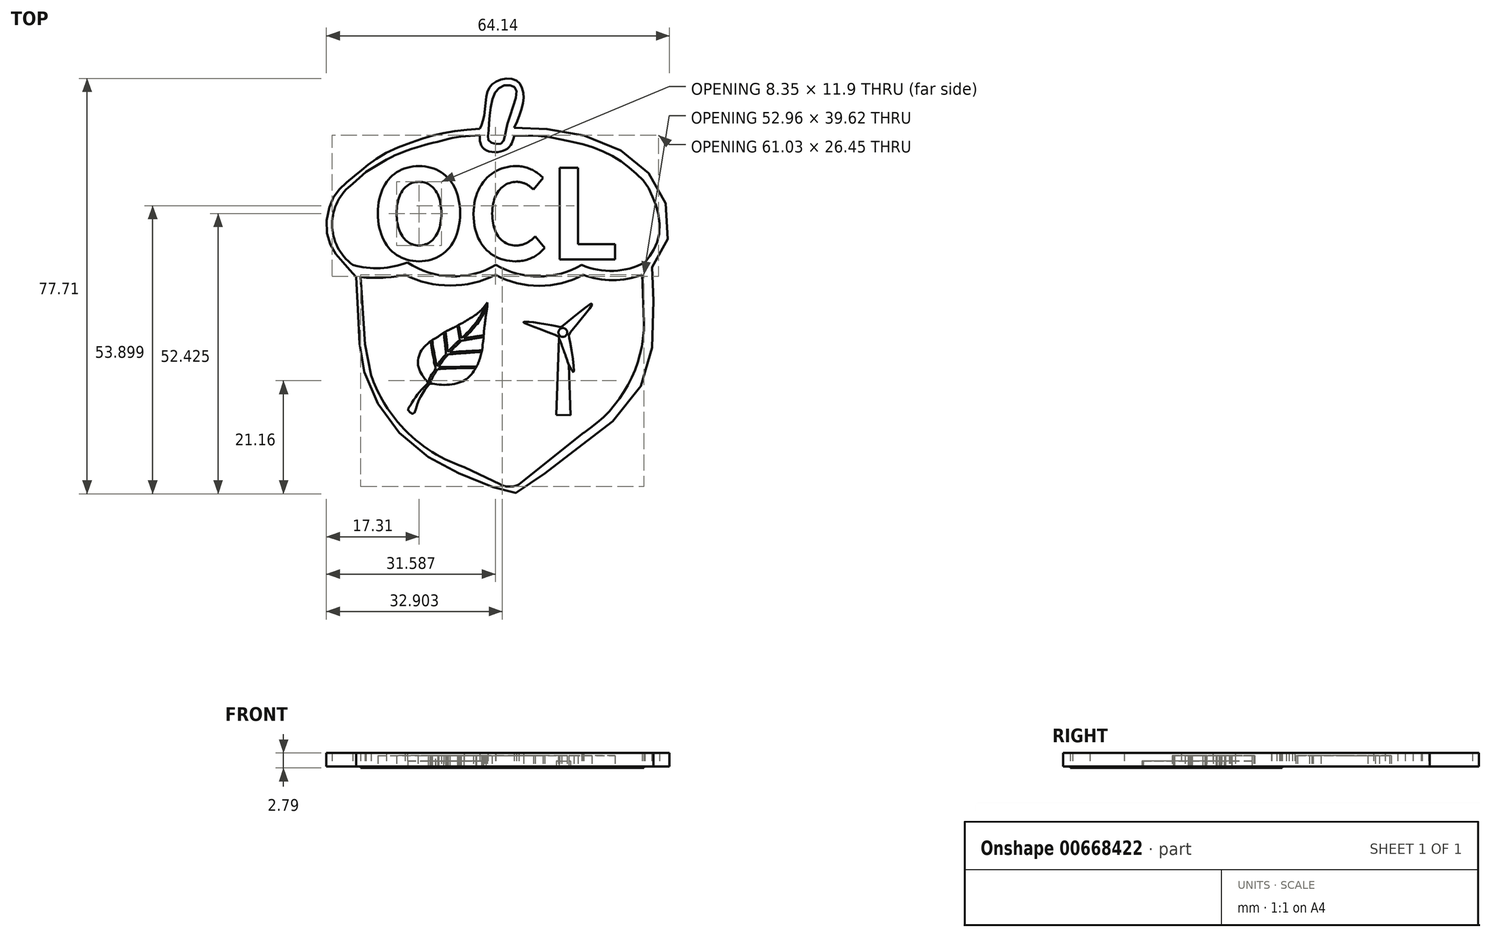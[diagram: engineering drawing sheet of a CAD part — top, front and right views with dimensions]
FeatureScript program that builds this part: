
annotation { "Feature Type Name" : "Feature", "Feature Type Description" : "" }
export const myFeature = defineFeature(function(context is Context, id is Id, definition is map)
    precondition{}
    {
        {
            var Q0;
            Q0=qCreatedBy(makeId("Top.planeOp"),FACE);
            var sketch = newSketch(context, id + "F0", { "sketchPlane" : qUnion([Q0])});
            skArc(sketch, "E0", {"start": v(-20.28, 3.7) * mm, "mid": v(-15.12, 3.1) * mm, "end": v(-10.03, 4.16) * mm});
            skArc(sketch, "E1", {"start": v(-10.03, 4.16) * mm, "mid": v(-1.85, 1.55) * mm, "end": v(6.48, 3.69) * mm});
            skArc(sketch, "E2", {"start": v(6.48, 3.69) * mm, "mid": v(14.5, 1.53) * mm, "end": v(22.52, 3.69) * mm});
            skArc(sketch, "E3", {"start": v(22.52, 3.69) * mm, "mid": v(28.49, 2.57) * mm, "end": v(34.35, 4.16) * mm});
            skArc(sketch, "E4", {"start": v(22.76, 1.83) * mm, "mid": v(28.27, 0.82) * mm, "end": v(33.78, 1.83) * mm});
            skArc(sketch, "E5", {"start": v(6.39, 1.83) * mm, "mid": v(14.58, -0.23) * mm, "end": v(22.76, 1.83) * mm});
            skArc(sketch, "E6", {"start": v(-10.53, 1.83) * mm, "mid": v(-2.07, -0.17) * mm, "end": v(6.39, 1.83) * mm});
            skArc(sketch, "E7", {"start": v(-18.8, 1.4) * mm, "mid": v(-14.65, 1.32) * mm, "end": v(-10.53, 1.83) * mm});
            skLineSegment(sketch, "E8", {"start": v(-18.8, 1.4) * mm, "end": v(-18.02, -11.17) * mm});
            skLineSegment(sketch, "E9", {"start": v(-18.02, -11.17) * mm, "end": v(-16.84, -17.03) * mm});
            skArc(sketch, "E10", {"start": v(-16.84, -17.03) * mm, "mid": v(-14.77, -21.58) * mm, "end": v(-11.9, -25.68) * mm});
            skArc(sketch, "E11", {"start": v(-11.9, -25.68) * mm, "mid": v(-6.27, -30.78) * mm, "end": v(0.55, -34.12) * mm});
            skLineSegment(sketch, "E12", {"start": v(0.55, -34.12) * mm, "end": v(7.32, -37.4) * mm});
            skArc(sketch, "E13", {"start": v(7.32, -37.4) * mm, "mid": v(9.03, -37.8) * mm, "end": v(10.74, -37.4) * mm});
            skLineSegment(sketch, "E14", {"start": v(10.74, -37.4) * mm, "end": v(22.9, -27.7) * mm});
            skArc(sketch, "E15", {"start": v(22.9, -27.7) * mm, "mid": v(31.17, -18.75) * mm, "end": v(34.16, -6.94) * mm});
            skLineSegment(sketch, "E16", {"start": v(33.78, 1.83) * mm, "end": v(34.16, -6.94) * mm});
            skArc(sketch, "E17", {"start": v(-20.28, 18.87) * mm, "mid": v(-24.15, 11.28) * mm, "end": v(-20.28, 3.7) * mm});
            skLineSegment(sketch, "E18", {"start": v(-20.28, 18.87) * mm, "end": v(-17.8, 21.07) * mm});
            skLineSegment(sketch, "E19", {"start": v(-17.8, 21.07) * mm, "end": v(-13.98, 23.39) * mm});
            skFitSpline(sketch, "E20", {"points": [v(-13.98, 23.39) * mm, v(-12, 24.37) * mm, v(-7.62, 25.92) * mm, v(-4.32, 26.78) * mm, v(-1.06, 27.54) * mm, v(3.49, 27.99) * mm], "startDerivative": vector(11.01, 5.92) * mm, "endDerivative": vector(20.96, 1.4) * mm});
            skFitSpline(sketch, "E21", {"points": [v(3.49, 27.99) * mm, v(3.49, 26.74) * mm, v(4.42, 25.26) * mm, v(6.72, 24.8) * mm, v(8.68, 25.49) * mm, v(9.58, 26.8) * mm, v(9.87, 27.8) * mm], "startDerivative": vector(-0.96, -8.3) * mm, "endDerivative": vector(1.6, 7.31) * mm});
            skFitSpline(sketch, "E22", {"points": [v(9.87, 27.8) * mm, v(14.71, 27.8) * mm, v(19.4, 27.02) * mm, v(23.33, 26.1) * mm, v(26.75, 24.8) * mm, v(29.85, 23.09) * mm, v(32.46, 20.99) * mm, v(34.55, 18.83) * mm, v(35.84, 16.22) * mm, v(36.68, 13.83) * mm, v(37.06, 10.39) * mm, v(36.5, 7.7) * mm, v(35.58, 5.87) * mm, v(34.35, 4.16) * mm], "startDerivative": vector(51.65, 2.21) * mm, "endDerivative": vector(-20.96, -27.35) * mm});
            skFitSpline(sketch, "E23", {"points": [v(5.3, 31.63) * mm, v(5.06, 28.28) * mm, v(5.06, 27.04) * mm, v(6.2, 26.35) * mm, v(7.62, 26.52) * mm, v(8.19, 27.89) * mm, v(8.7, 30.33) * mm, v(10.29, 35.6) * mm, v(9.83, 37.03) * mm, v(7.96, 37.25) * mm, v(6.26, 35.78) * mm, v(5.3, 31.63) * mm]});
            skPoint(sketch, "E24.11.internal.orphan", {"position": v(-1.38, -8.15) * mm});
            skFitSpline(sketch, "E25", {"points": [v(-5.8, -18.5) * mm, v(-5.02, -18.6) * mm, v(-4.25, -18.68) * mm, v(-3.06, -18.75) * mm, v(-2.01, -18.67) * mm, v(-1.04, -18.5) * mm, v(-0.29, -18.28) * mm, v(0.44, -17.97) * mm, v(1, -17.62) * mm, v(1.59, -17.1) * mm, v(2.18, -16.42) * mm, v(2.5, -15.96) * mm, v(2.87, -15.3) * mm, v(3.16, -14.67) * mm, v(3.42, -13.95) * mm, v(3.62, -13.3) * mm, v(3.8, -12.62) * mm, v(3.95, -11.88) * mm, v(4, -11.07) * mm], "startDerivative": vector(14.5, -1.6) * mm, "endDerivative": vector(0.27, 14.6) * mm});
            skFitSpline(sketch, "E26", {"points": [v(4, -11.07) * mm, v(4.13, -10.32) * mm, v(4.19, -9.56) * mm, v(4.23, -8.81) * mm, v(4.33, -7.77) * mm], "startDerivative": vector(0.64, 3.1) * mm, "endDerivative": vector(0.44, 3.86) * mm});
            skFitSpline(sketch, "E27", {"points": [v(4.33, -7.77) * mm, v(4.47, -6.77) * mm, v(4.58, -5.82) * mm, v(4.79, -4.61) * mm, v(4.89, -3.36) * mm], "startDerivative": vector(0.64, 4.27) * mm, "endDerivative": vector(0.24, 4.7) * mm});
            skFitSpline(sketch, "E28", {"points": [v(4.89, -3.36) * mm, v(4.13, -4.35) * mm, v(3.47, -5.03) * mm, v(2.5, -5.78) * mm, v(1.56, -6.37) * mm, v(0.57, -6.97) * mm, v(-0.4, -7.5) * mm, v(-1.11, -7.89) * mm, v(-1.93, -8.3) * mm, v(-2.96, -8.8) * mm, v(-3.88, -9.4) * mm, v(-4.27, -9.67) * mm, v(-5.4, -10.36) * mm, v(-6.45, -11.17) * mm, v(-7.35, -12.14) * mm, v(-7.83, -13.14) * mm, v(-8.12, -14.38) * mm, v(-7.89, -15.8) * mm, v(-7.44, -16.72) * mm, v(-6.63, -17.85) * mm, v(-6.17, -18.34) * mm], "startDerivative": vector(-14.5, -19.64) * mm, "endDerivative": vector(10.8, -10.65) * mm});
            skFitSpline(sketch, "E29", {"points": [v(-6.17, -18.34) * mm, v(-6.63, -18.84) * mm, v(-7.22, -19.44) * mm, v(-7.69, -19.94) * mm, v(-8.12, -20.45) * mm, v(-8.54, -21.05) * mm, v(-9, -21.68) * mm, v(-9.3, -22.24) * mm, v(-9.72, -22.87) * mm, v(-10, -23.29) * mm, v(-9.74, -23.78) * mm, v(-9.3, -24.1) * mm, v(-8.85, -24.1) * mm, v(-8.54, -23.36) * mm, v(-8, -21.8) * mm, v(-7.57, -20.89) * mm, v(-7, -19.94) * mm, v(-6.45, -19.16) * mm, v(-6.1, -18.73) * mm, v(-5.92, -18.5) * mm, v(-5.8, -18.5) * mm], "startDerivative": vector(-8.63, -10.09) * mm, "endDerivative": vector(5.67, -1.33) * mm});
            skFitSpline(sketch, "E30", {"points": [v(-5.4, -10.36) * mm, v(-5.28, -11.6) * mm, v(-5.14, -12.36) * mm, v(-5.05, -12.92) * mm, v(-4.92, -13.66) * mm, v(-4.73, -14.38) * mm, v(-4.52, -15.15) * mm, v(-4.12, -14.6) * mm, v(-3.6, -13.83) * mm, v(-2.84, -13.04) * mm], "startDerivative": vector(0.8, -9.62) * mm, "endDerivative": vector(6.24, 6.35) * mm});
            skFitSpline(sketch, "E31", {"points": [v(-2.84, -13.04) * mm, v(-2.96, -11.87) * mm, v(-3.06, -10.82) * mm, v(-3.2, -9.85) * mm, v(-3.26, -8.98) * mm], "startDerivative": vector(-0.43, 4.4) * mm, "endDerivative": vector(-0.13, 3.64) * mm});
            skFitSpline(sketch, "E32", {"points": [v(-5.7, -10.56) * mm, v(-5.6, -11.65) * mm, v(-5.4, -12.76) * mm, v(-5.28, -13.34) * mm, v(-5.16, -13.92) * mm, v(-5.05, -14.81) * mm, v(-4.85, -15.22) * mm, v(-4.84, -15.74) * mm, v(-5.17, -16.33) * mm, v(-5.8, -17.23) * mm, v(-6.17, -18.34) * mm], "startDerivative": vector(0.6, -9.1) * mm, "endDerivative": vector(-2.29, -9.49) * mm});
            skFitSpline(sketch, "E33", {"points": [v(-2.56, -12.55) * mm, v(-2.62, -11.86) * mm, v(-2.68, -11.11) * mm, v(-2.76, -10.36) * mm, v(-2.84, -9.69) * mm, v(-2.96, -8.8) * mm], "startDerivative": vector(-0.3, 3.57) * mm, "endDerivative": vector(-0.55, 4.21) * mm});
            skFitSpline(sketch, "E34", {"points": [v(-2.56, -12.55) * mm, v(-1.92, -11.93) * mm, v(-1.55, -11.51) * mm, v(-1.08, -11.05) * mm, v(-0.32, -10.35) * mm], "startDerivative": vector(2.6, 2.4) * mm, "endDerivative": vector(2.8, 2.54) * mm});
            skFitSpline(sketch, "E35", {"points": [v(-0.03, -10) * mm, v(-0.16, -9.17) * mm, v(-0.23, -8.78) * mm, v(-0.33, -8.26) * mm, v(-0.5, -7.56) * mm], "startDerivative": vector(-0.52, 3.08) * mm, "endDerivative": vector(-0.68, 2.63) * mm});
            skFitSpline(sketch, "E36", {"points": [v(-0.03, -10) * mm, v(0.58, -9.53) * mm, v(0.97, -9.1) * mm, v(1.45, -8.64) * mm, v(1.96, -8.03) * mm, v(2.81, -7.06) * mm, v(3.13, -6.52) * mm, v(3.6, -5.83) * mm, v(4.05, -4.93) * mm, v(4.63, -3.87) * mm], "startDerivative": vector(6.2, 4.35) * mm, "endDerivative": vector(4.64, 8.07) * mm});
            skFitSpline(sketch, "E37", {"points": [v(4.63, -3.87) * mm, v(4.63, -4.45) * mm, v(4.43, -5) * mm, v(3.5, -6.63) * mm, v(2.8, -7.55) * mm, v(2.29, -8.17) * mm, v(1.72, -8.84) * mm, v(1.13, -9.38) * mm, v(0.5, -10.02) * mm], "startDerivative": vector(0.36, -6.12) * mm, "endDerivative": vector(-5.12, -5.34) * mm});
            skFitSpline(sketch, "E38", {"points": [v(0.5, -10.02) * mm, v(1.23, -9.91) * mm, v(1.96, -9.82) * mm, v(3.03, -9.65) * mm, v(4.2, -9.47) * mm], "startDerivative": vector(3.32, 0.49) * mm, "endDerivative": vector(4.08, 0.62) * mm});
            skFitSpline(sketch, "E39", {"points": [v(4.17, -9.83) * mm, v(2.73, -10.02) * mm, v(1.63, -10.23) * mm, v(0.98, -10.32) * mm, v(-0.04, -10.53) * mm], "startDerivative": vector(-4.96, -0.57) * mm, "endDerivative": vector(-4.39, -0.97) * mm});
            skFitSpline(sketch, "E40", {"points": [v(-0.04, -10.53) * mm, v(-0.66, -11.16) * mm, v(-1.09, -11.55) * mm, v(-1.53, -12) * mm, v(-2.15, -12.67) * mm], "startDerivative": vector(-2.37, -2.49) * mm, "endDerivative": vector(-2.33, -2.53) * mm});
            skFitSpline(sketch, "E41", {"points": [v(-2.15, -12.67) * mm, v(-1.08, -12.59) * mm, v(-0.3, -12.5) * mm, v(0.58, -12.48) * mm, v(1.2, -12.44) * mm, v(1.66, -12.4) * mm, v(2.36, -12.37) * mm, v(3.21, -12.33) * mm, v(3.88, -12.29) * mm], "startDerivative": vector(7.47, 0.4) * mm, "endDerivative": vector(5.38, 0.46) * mm});
            skFitSpline(sketch, "E42", {"points": [v(3.81, -12.58) * mm, v(2.96, -12.62) * mm, v(2.37, -12.67) * mm, v(1.7, -12.71) * mm, v(1.1, -12.76) * mm, v(0.5, -12.8) * mm, v(-0.1, -12.84) * mm, v(-0.99, -12.91) * mm, v(-1.74, -12.98) * mm, v(-2.46, -13.05) * mm], "startDerivative": vector(-7.27, -0.36) * mm, "endDerivative": vector(-6.4, -0.65) * mm});
            skFitSpline(sketch, "E43", {"points": [v(-2.46, -13.05) * mm, v(-2.78, -13.4) * mm, v(-3.16, -13.83) * mm, v(-3.6, -14.43) * mm, v(-3.91, -14.95) * mm, v(-4.21, -15.41) * mm], "startDerivative": vector(-1.72, -1.94) * mm, "endDerivative": vector(-1.55, -2.36) * mm});
            skFitSpline(sketch, "E44", {"points": [v(-4.21, -15.41) * mm, v(-2.79, -15.41) * mm, v(-1.08, -15.41) * mm, v(0.33, -15.36) * mm, v(2.28, -15.36) * mm, v(2.84, -15.35) * mm], "startDerivative": vector(6.7, 0.03) * mm, "endDerivative": vector(3.53, 0.04) * mm});
            skFitSpline(sketch, "E45", {"points": [v(2.72, -15.57) * mm, v(0.54, -15.6) * mm, v(-0.8, -15.63) * mm, v(-1.98, -15.67) * mm, v(-3.5, -15.75) * mm, v(-4.43, -15.79) * mm], "startDerivative": vector(-9.25, -0.12) * mm, "endDerivative": vector(-5.28, -0.17) * mm});
            skFitSpline(sketch, "E46", {"points": [v(-4.43, -15.79) * mm, v(-4.97, -16.69) * mm, v(-5.35, -17.36) * mm, v(-5.84, -18.5) * mm], "startDerivative": vector(-1.65, -2.8) * mm, "endDerivative": vector(-1.34, -3.34) * mm});
            skLineSegment(sketch, "E47", {"start": v(-0.73, -7.68) * mm, "end": v(-0.73, -7.68) * mm});
            skLineSegment(sketch, "E48", {"start": v(-5.84, -18.5) * mm, "end": v(-5.84, -18.5) * mm});
            skLineSegment(sketch, "E49", {"start": v(-0.7, -7.67) * mm, "end": v(-0.32, -10.35) * mm});
            skLineSegment(sketch, "E50", {"start": v(-0.7, -7.67) * mm, "end": v(-0.7, -7.67) * mm});
            skLineSegment(sketch, "E51", {"start": v(-20.28, 3.7) * mm, "end": v(-18.8, 1.4) * mm});
            skLineSegment(sketch, "E52", {"start": v(34.35, 4.16) * mm, "end": v(33.78, 1.83) * mm});
            skFitSpline(sketch, "E53", {"points": [v(3.49, 29.16) * mm, v(-1.36, 28.7) * mm, v(-5.01, 27.99) * mm, v(-8.62, 26.87) * mm, v(-13.58, 24.9) * mm, v(-16.85, 22.85) * mm, v(-18.62, 21.46) * mm, v(-20.64, 19.76) * mm, v(-23.05, 17.55) * mm, v(-24.52, 14.94) * mm, v(-25.18, 9.97) * mm, v(-23.81, 6.28) * mm, v(-21.63, 3.61) * mm, v(-19.62, 1.4) * mm], "startDerivative": vector(-56.46, -4.2) * mm, "endDerivative": vector(28.25, -31.34) * mm});
            skPoint(sketch, "E54.5.internal.snap0", {"position": v(-14.77, -21.58) * mm});
            skFitSpline(sketch, "E54", {"points": [v(-19.62, 1.4) * mm, v(-19.38, -3.12) * mm, v(-19.15, -8.63) * mm, v(-18.8, -13.32) * mm, v(-18.02, -16.7) * mm, v(-15.99, -21.58) * mm, v(-12.7, -26.44) * mm, v(-8.11, -30.88) * mm, v(-3, -34.12) * mm, v(1.67, -36.13) * mm, v(7.35, -38.51) * mm, v(9.4, -39.14) * mm, v(11.75, -38.13) * mm, v(17.92, -33.58) * mm, v(23.62, -29.17) * mm, v(31, -22.9) * mm, v(34.86, -15.67) * mm, v(35.9, -8.21) * mm, v(35.66, 1.4) * mm, v(35.82, 3.7) * mm, v(38.4, 7.93) * mm, v(38.56, 13.83) * mm, v(36.5, 18.82) * mm, v(32.83, 23.09) * mm, v(27.32, 26.31) * mm, v(20.56, 28.47) * mm, v(14.72, 29.2) * mm, v(9.9, 29.38) * mm], "startDerivative": vector(7.5, -131.86) * mm, "endDerivative": vector(-137.8, 3) * mm});
            skFitSpline(sketch, "E55", {"points": [v(9.9, 29.38) * mm, v(11.49, 33.6) * mm, v(11.49, 36.3) * mm, v(10.29, 38.2) * mm, v(7.47, 38.4) * mm, v(5.45, 37.12) * mm, v(4.64, 34.95) * mm, v(4.16, 31.1) * mm, v(3.49, 29.16) * mm], "startDerivative": vector(12.46, 27.9) * mm, "endDerivative": vector(-7.13, -15.96) * mm});
            skText(sketch, "E56", { "text": "OCL", "fontName": "NotoSansCJKjp-Bold.otf"});
            skLineSegment(sketch, "E57", {"start": v(6.39, 1.83) * mm, "end": v(7.32, -37.4) * mm});
            skLineSegment(sketch, "E58", {"start": v(18.28, -10.01) * mm, "end": v(17.77, -24.34) * mm});
            skLineSegment(sketch, "E59", {"start": v(17.77, -24.34) * mm, "end": v(20.4, -24.43) * mm});
            skLineSegment(sketch, "E60", {"start": v(20.4, -24.43) * mm, "end": v(20.1, -15.03) * mm});
            skFitSpline(sketch, "E61", {"points": [v(20.1, -15.03) * mm, v(20.8, -16.2) * mm, v(20.93, -16.35) * mm, v(21, -16.33) * mm, v(21.04, -16.05) * mm, v(20.86, -13.88) * mm, v(20.26, -10.38) * mm, v(20.1, -9.66) * mm, v(20.1, -9.38) * mm, v(20.75, -8.48) * mm, v(21.8, -7.2) * mm, v(23.49, -5.14) * mm, v(24.39, -3.84) * mm, v(24.42, -3.61) * mm, v(24.36, -3.56) * mm, v(24.14, -3.62) * mm, v(23.74, -3.87) * mm, v(21.18, -5.91) * mm, v(18.78, -7.84) * mm], "startDerivative": vector(13.18, -22.09) * mm, "endDerivative": vector(-22.7, -18.2) * mm});
            skFitSpline(sketch, "E62", {"points": [v(18.78, -7.84) * mm, v(18.63, -7.92) * mm, v(18.3, -7.88) * mm, v(12.8, -6.97) * mm, v(11.75, -6.97) * mm, v(11.63, -7) * mm, v(11.66, -7.07) * mm, v(12.14, -7.34) * mm, v(17.26, -9.28) * mm, v(18.1, -9.65) * mm, v(18.28, -9.78) * mm, v(18.28, -10.01) * mm], "startDerivative": vector(-3.67, -2.5) * mm, "endDerivative": vector(-0.87, -5.3) * mm});
            skFitSpline(sketch, "E63", {"points": [v(18.28, -10.01) * mm, v(18.54, -10.67) * mm, v(20.1, -15.03) * mm], "startDerivative": vector(0.76, -1.8) * mm, "endDerivative": vector(2.61, -7.4) * mm});
            skCircle(sketch, "E64", {"center": v(18.98, -8.94) * mm, "radius": 0.83 * mm});
            skCircle(sketch, "E65", {"center": v(18.98, -8.94) * mm, "radius": 0.67 * mm});
            const initialGuessF0  = {"E56": [-0.01684, 0.00469, 1, 0, 0.0167]};
            skSetInitialGuess(sketch, initialGuessF0);
            skSolve(sketch);
        }
        {
            var Q0;
            Q0=makeQuery(id+"F0.imprint","IMPRINT",FACE,{"disambiguationData":[TD([[makeQuery(id+"F0.imprint","IMPRINT",EDGE,{"derivedFrom":sQuery(id+"F0.wireOp",EDGE,"E0")}),-1.0]])]});
            extrude(context, id + "F1", {"entities" : qUnion([Q0]), "depth" : 2.03 * mm, "offsetDistance" : 25.4 * mm});
        }
        {
            var Q0;
            Q0=makeQuery(id+"F0.imprint","IMPRINT",FACE,{"disambiguationData":[TD([[makeQuery(id+"F0.imprint","IMPRINT",EDGE,{"derivedFrom":sQuery(id+"F0.wireOp",EDGE,"E56.sketch_text.stroke-0")}),1.0]])]});
            var Q1;
            Q1=makeQuery(id+"F0.imprint","IMPRINT",FACE,{"disambiguationData":[TD([[makeQuery(id+"F0.imprint","IMPRINT",EDGE,{"derivedFrom":sQuery(id+"F0.wireOp",EDGE,"E56.sketch_text.stroke-8")}),1.0]])]});
            var Q2;
            Q2=makeQuery(id+"F0.imprint","IMPRINT",FACE,{"disambiguationData":[TD([[makeQuery(id+"F0.imprint","IMPRINT",EDGE,{"derivedFrom":sQuery(id+"F0.wireOp",EDGE,"E56.sketch_text.stroke-18")}),1.0]])]});
            extrude(context, id + "F2", {"entities" : qUnion([Q0, Q1, Q2]), "depth" : 2.03 * mm, "offsetDistance" : 25.4 * mm});
        }
        {
            var Q0;
            Q0=makeQuery(id+"F0.imprint","IMPRINT",FACE,{"disambiguationData":[TD([[makeQuery(id+"F0.imprint","IMPRINT",EDGE,{"derivedFrom":sQuery(id+"F0.wireOp",EDGE,"E8")}),-1.0]])]});
            extrude(context, id + "F3", {"entities" : qUnion([Q0]), "operationType" : NewBodyOperationType.ADD, "depth" : 2.54 * mm, "offsetDistance" : 25.4 * mm});
        }
        {
            var Q0;
            Q0=makeQuery(id+"F0.imprint","IMPRINT",FACE,{"disambiguationData":[TD([[makeQuery(id+"F0.imprint","IMPRINT",EDGE,{"derivedFrom":sQuery(id+"F0.wireOp",EDGE,"E0")}),-1.0]])]});
            extrude(context, id + "F4", {"entities" : qUnion([Q0]), "operationType" : NewBodyOperationType.ADD, "depth" : 2.54 * mm, "offsetDistance" : 25.4 * mm});
        }
        {
            var Q0;
            {var subQ0=sQuery(id+"F0.wireOp",EDGE,"E32");Q0=makeQuery(id+"F0.imprint","IMPRINT",FACE,{"disambiguationData":[TD([[makeQuery(id+"F0.imprint","IMPRINT",EDGE,{"derivedFrom":subQ0}),-1.0]])]});}
            var Q1;
            {var subQ0=sQuery(id+"F0.wireOp",EDGE,"E30");Q1=makeQuery(id+"F0.imprint","IMPRINT",FACE,{"disambiguationData":[TD([[makeQuery(id+"F0.imprint","IMPRINT",EDGE,{"derivedFrom":subQ0}),1.0]])]});}
            var Q2;
            {var subQ0=sQuery(id+"F0.wireOp",EDGE,"E33");Q2=makeQuery(id+"F0.imprint","IMPRINT",FACE,{"disambiguationData":[TD([[makeQuery(id+"F0.imprint","IMPRINT",EDGE,{"derivedFrom":subQ0}),-1.0]])]});}
            var Q3;
            {var subQ2=sQuery(id+"F0.wireOp",EDGE,"E27");Q3=makeQuery(id+"F0.imprint","IMPRINT",FACE,{"disambiguationData":[TD([[makeQuery(id+"F0.imprint","IMPRINT",EDGE,{"derivedFrom":subQ2}),1.0]])]});}
            var Q4;
            {var subQ0=sQuery(id+"F0.wireOp",EDGE,"E39");Q4=makeQuery(id+"F0.imprint","IMPRINT",FACE,{"disambiguationData":[TD([[makeQuery(id+"F0.imprint","IMPRINT",EDGE,{"derivedFrom":subQ0}),1.0]])]});}
            var Q5;
            {var subQ0=sQuery(id+"F0.wireOp",EDGE,"E42");Q5=makeQuery(id+"F0.imprint","IMPRINT",FACE,{"disambiguationData":[TD([[makeQuery(id+"F0.imprint","IMPRINT",EDGE,{"derivedFrom":subQ0}),1.0]])]});}
            var Q6;
            {var subQ0=sQuery(id+"F0.wireOp",EDGE,"E45");Q6=makeQuery(id+"F0.imprint","IMPRINT",FACE,{"disambiguationData":[TD([[makeQuery(id+"F0.imprint","IMPRINT",EDGE,{"derivedFrom":subQ0}),1.0]])]});}
            extrude(context, id + "F5", {"entities" : qUnion([Q0, Q1, Q2, Q3, Q4, Q5, Q6]), "depth" : 2.03 * mm, "offsetDistance" : 25.4 * mm});
        }
        {
            var Q0;
            {var subQ16=sQuery(id+"F0.wireOp",EDGE,"E30");Q0=makeQuery(id+"F0.imprint","IMPRINT",FACE,{"disambiguationData":[TD([[makeQuery(id+"F0.imprint","IMPRINT",EDGE,{"derivedFrom":subQ16}),-1.0]])]});}
            extrude(context, id + "F6", {"entities" : qUnion([Q0]), "depth" : 1.02 * mm, "offsetDistance" : 25.4 * mm});
        }
        {
            var Q0;
            Q0=makeQuery(id+"F0.imprint","IMPRINT",FACE,{"disambiguationData":[TD([[makeQuery(id+"F0.imprint","IMPRINT",EDGE,{"derivedFrom":sQuery(id+"F0.wireOp",EDGE,"E61")}),1.0]])]});
            extrude(context, id + "F7", {"entities" : qUnion([Q0]), "depth" : 2.03 * mm, "offsetDistance" : 25.4 * mm});
        }
        {
            var Q0;
            Q0=makeQuery(id+"F0.imprint","IMPRINT",FACE,{"disambiguationData":[TD([[makeQuery(id+"F0.imprint","IMPRINT",EDGE,{"derivedFrom":sQuery(id+"F0.wireOp",EDGE,"E58")}),1.0]])]});
            extrude(context, id + "F8", {"entities" : qUnion([Q0]), "operationType" : NewBodyOperationType.ADD, "depth" : 1.02 * mm, "offsetDistance" : 25.4 * mm});
        }
        {
            var Q0;
            {var subQ0=sQuery(id+"F0.wireOp",EDGE,"E52");var subQ1=sQuery(id+"F0.wireOp",EDGE,"E51");Q0=makeQuery(id+"F3.boolean.opBoolean","MERGE",FACE,{"derivedFrom":[makeQuery(id+"F1.opExtrude","CAP_FACE",FACE,{"disambiguationData":[OSD([sQuery(id+"F0.wireOp",EDGE,"E0"),sQuery(id+"F0.wireOp",EDGE,"E1"),sQuery(id+"F0.wireOp",EDGE,"E2"),sQuery(id+"F0.wireOp",EDGE,"E3"),sQuery(id+"F0.wireOp",EDGE,"E4"),sQuery(id+"F0.wireOp",EDGE,"E5"),sQuery(id+"F0.wireOp",EDGE,"E6"),sQuery(id+"F0.wireOp",EDGE,"E7"),subQ1,subQ0])],"isStart":true}),makeQuery(id+"F3.opExtrude","CAP_FACE",FACE,{"disambiguationData":[OSD([sQuery(id+"F0.wireOp",EDGE,"E8"),sQuery(id+"F0.wireOp",EDGE,"E9"),sQuery(id+"F0.wireOp",EDGE,"E10"),sQuery(id+"F0.wireOp",EDGE,"E11"),sQuery(id+"F0.wireOp",EDGE,"E12"),sQuery(id+"F0.wireOp",EDGE,"E13"),sQuery(id+"F0.wireOp",EDGE,"E14"),sQuery(id+"F0.wireOp",EDGE,"E15"),sQuery(id+"F0.wireOp",EDGE,"E16"),sQuery(id+"F0.wireOp",EDGE,"E17"),sQuery(id+"F0.wireOp",EDGE,"E18"),sQuery(id+"F0.wireOp",EDGE,"E19"),sQuery(id+"F0.wireOp",EDGE,"E20"),sQuery(id+"F0.wireOp",EDGE,"E21"),sQuery(id+"F0.wireOp",EDGE,"E22"),sQuery(id+"F0.wireOp",EDGE,"E23"),subQ1,subQ0,sQuery(id+"F0.wireOp",EDGE,"E53"),sQuery(id+"F0.wireOp",EDGE,"E54"),sQuery(id+"F0.wireOp",EDGE,"E55")])],"isStart":true})]});}
            var sketch = newSketch(context, id + "F9", { "sketchPlane" : qUnion([Q0])});
            skSolve(sketch);
        }
        {
            var Q0;
            Q0 = qSketchRegion(id + "F9", true);
            var Q1;
            Q1=makeQuery(id+"F9.imprint","IMPRINT",FACE,{"disambiguationData":[TD([[makeQuery(id+"F9.imprint","IMPRINT",EDGE,{"derivedFrom":makeQuery(id+"F1.opExtrude","CAP_EDGE",EDGE,{"disambiguationData":[OSD([sQuery(id+"F0.wireOp",EDGE,"E4")])],"isStart":true})}),1.0]])]});
            extrude(context, id + "F10", {"entities" : qUnion([Q0, Q1]), "depth" : 0.25 * mm, "offsetDistance" : 25.4 * mm});
        }
    });
